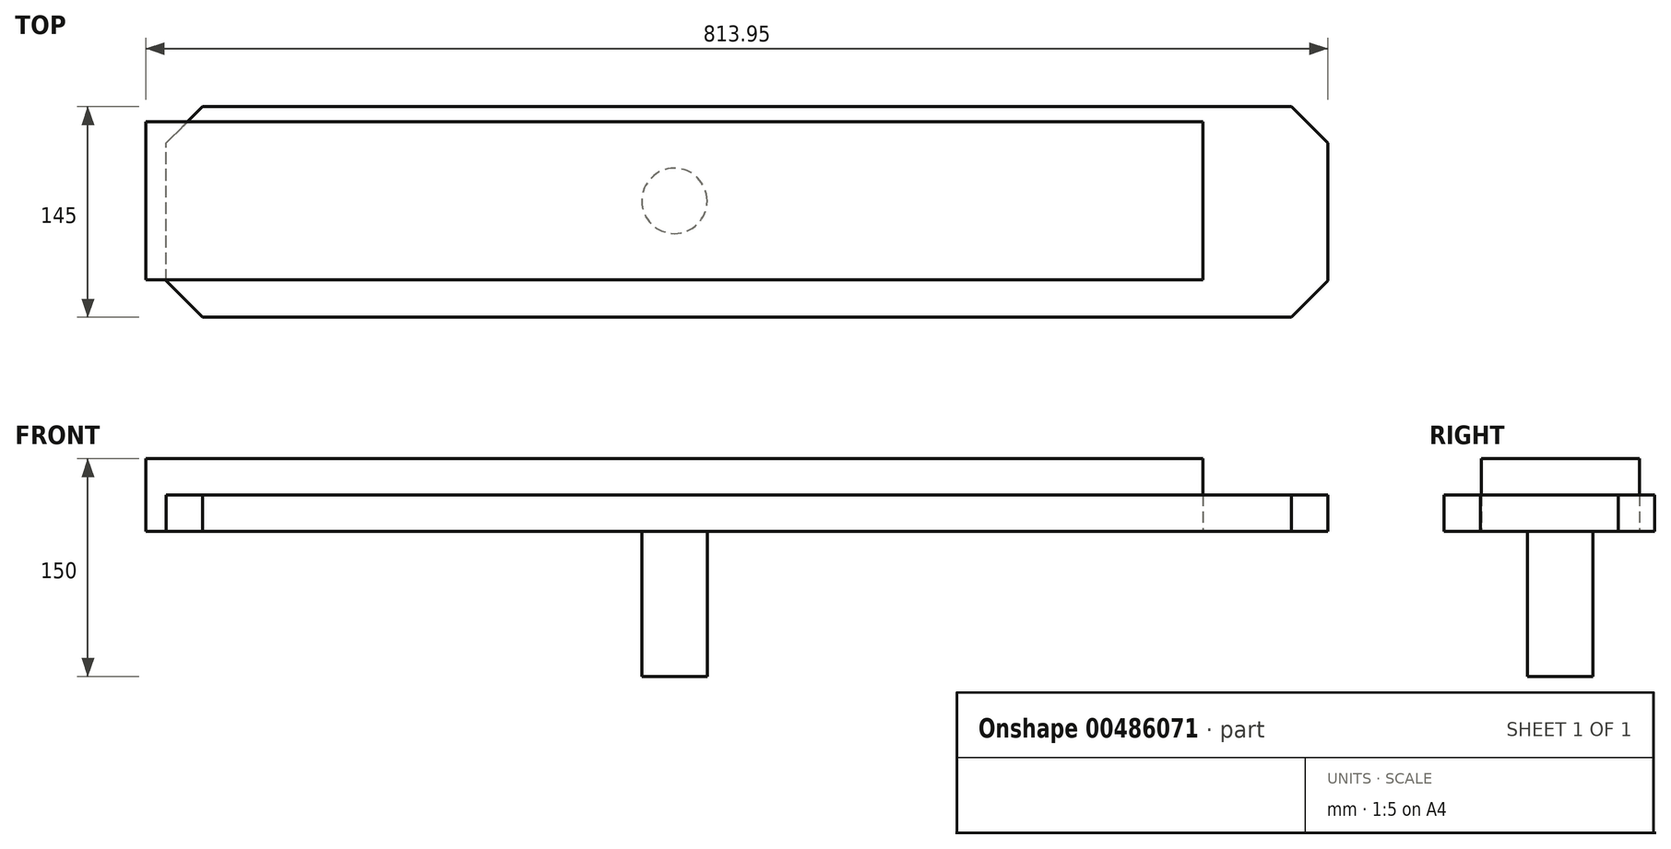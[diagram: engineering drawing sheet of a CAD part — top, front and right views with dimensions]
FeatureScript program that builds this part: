
annotation { "Feature Type Name" : "Feature", "Feature Type Description" : "" }
export const myFeature = defineFeature(function(context is Context, id is Id, definition is map)
    precondition{}
    {
        {
            var Q0;
            Q0=qCreatedBy(makeId("Top.planeOp"),FACE);
            var sketch = newSketch(context, id + "F0", { "sketchPlane" : qUnion([Q0])});
            skLineSegment(sketch, "E0.bottom", {"start": v(-384.42, -151.84) * mm, "end": v(415.58, -151.84) * mm});
            skLineSegment(sketch, "E0.top", {"start": v(-384.42, -6.84) * mm, "end": v(415.58, -6.84) * mm});
            skLineSegment(sketch, "E0.left", {"start": v(-384.42, -151.84) * mm, "end": v(-384.42, -6.84) * mm});
            skLineSegment(sketch, "E0.right", {"start": v(415.58, -151.84) * mm, "end": v(415.58, -6.84) * mm});
            skSolve(sketch);
        }
        {
            var Q0;
            Q0=qCreatedBy(makeId("Top.planeOp"),FACE);
            var sketch = newSketch(context, id + "F1", { "sketchPlane" : qUnion([Q0])});
            skLineSegment(sketch, "E1.bottom", {"start": v(-398.37, -126.22) * mm, "end": v(329.63, -126.22) * mm});
            skLineSegment(sketch, "E1.top", {"start": v(-398.37, -17.22) * mm, "end": v(329.63, -17.22) * mm});
            skLineSegment(sketch, "E1.left", {"start": v(-398.37, -126.22) * mm, "end": v(-398.37, -17.22) * mm});
            skLineSegment(sketch, "E1.right", {"start": v(329.63, -126.22) * mm, "end": v(329.63, -17.22) * mm});
            skCircle(sketch, "E2", {"center": v(-34.37, -71.72) * mm, "radius": 22.5 * mm});
            skPoint(sketch, "E3", {"position": v(-34.37, -17.22) * mm});
            skPoint(sketch, "E4", {"position": v(-34.37, -126.22) * mm});
            skLineSegment(sketch, "E5", {"start": v(-34.37, -17.22) * mm, "end": v(-34.37, -126.22) * mm, "construction": true});
            skSolve(sketch);
        }
        {
            var Q0;
            Q0=makeQuery(id+"F1.imprint","IMPRINT",FACE,{"disambiguationData":[TD([[makeQuery(id+"F1.imprint","IMPRINT",EDGE,{"derivedFrom":sQuery(id+"F1.wireOp",EDGE,"E1.bottom")}),1.0]])]});
            var Q1;
            Q1=makeQuery(id+"F1.imprint","IMPRINT",FACE,{"disambiguationData":[TD([[makeQuery(id+"F1.imprint","IMPRINT",EDGE,{"derivedFrom":sQuery(id+"F1.wireOp",EDGE,"E2")}),1.0]])]});
            extrude(context, id + "F2", {"entities" : qUnion([Q0, Q1]), "depth" : 50 * mm});
        }
        {
            var Q0;
            Q0=makeQuery(id+"F1.imprint","IMPRINT",FACE,{"disambiguationData":[TD([[makeQuery(id+"F1.imprint","IMPRINT",EDGE,{"derivedFrom":sQuery(id+"F1.wireOp",EDGE,"E2")}),1.0]])]});
            extrude(context, id + "F3", {"entities" : qUnion([Q0]), "operationType" : NewBodyOperationType.ADD, "oppositeDirection" : true, "depth" : 100 * mm});
        }
        {
            var Q0;
            Q0 = qSketchRegion(id + "F0", true);
            extrude(context, id + "F4", {"entities" : qUnion([Q0]), "depth" : 25 * mm});
        }
        {
            var Q0;
            Q0=makeQuery(id+"F4.opExtrude","SWEPT_EDGE",EDGE,{"disambiguationData":[OSD([sQuery(id+"F0.wireOp",EDGE,"E0.top"),sQuery(id+"F0.wireOp",EDGE,"E0.right")])]});
            var Q1;
            Q1=makeQuery(id+"F4.opExtrude","SWEPT_EDGE",EDGE,{"disambiguationData":[OSD([sQuery(id+"F0.wireOp",EDGE,"E0.bottom"),sQuery(id+"F0.wireOp",EDGE,"E0.right")])]});
            var Q2;
            Q2=makeQuery(id+"F4.opExtrude","SWEPT_EDGE",EDGE,{"disambiguationData":[OSD([sQuery(id+"F0.wireOp",EDGE,"E0.top"),sQuery(id+"F0.wireOp",EDGE,"E0.left")])]});
            var Q3;
            Q3=makeQuery(id+"F4.opExtrude","SWEPT_EDGE",EDGE,{"disambiguationData":[OSD([sQuery(id+"F0.wireOp",EDGE,"E0.bottom"),sQuery(id+"F0.wireOp",EDGE,"E0.left")])]});
            chamfer(context, id + "F5", {"entities" : qUnion([Q0, Q1, Q2, Q3]), "width" : 25 * mm, "tangentPropagation" : true});
        }
    });
